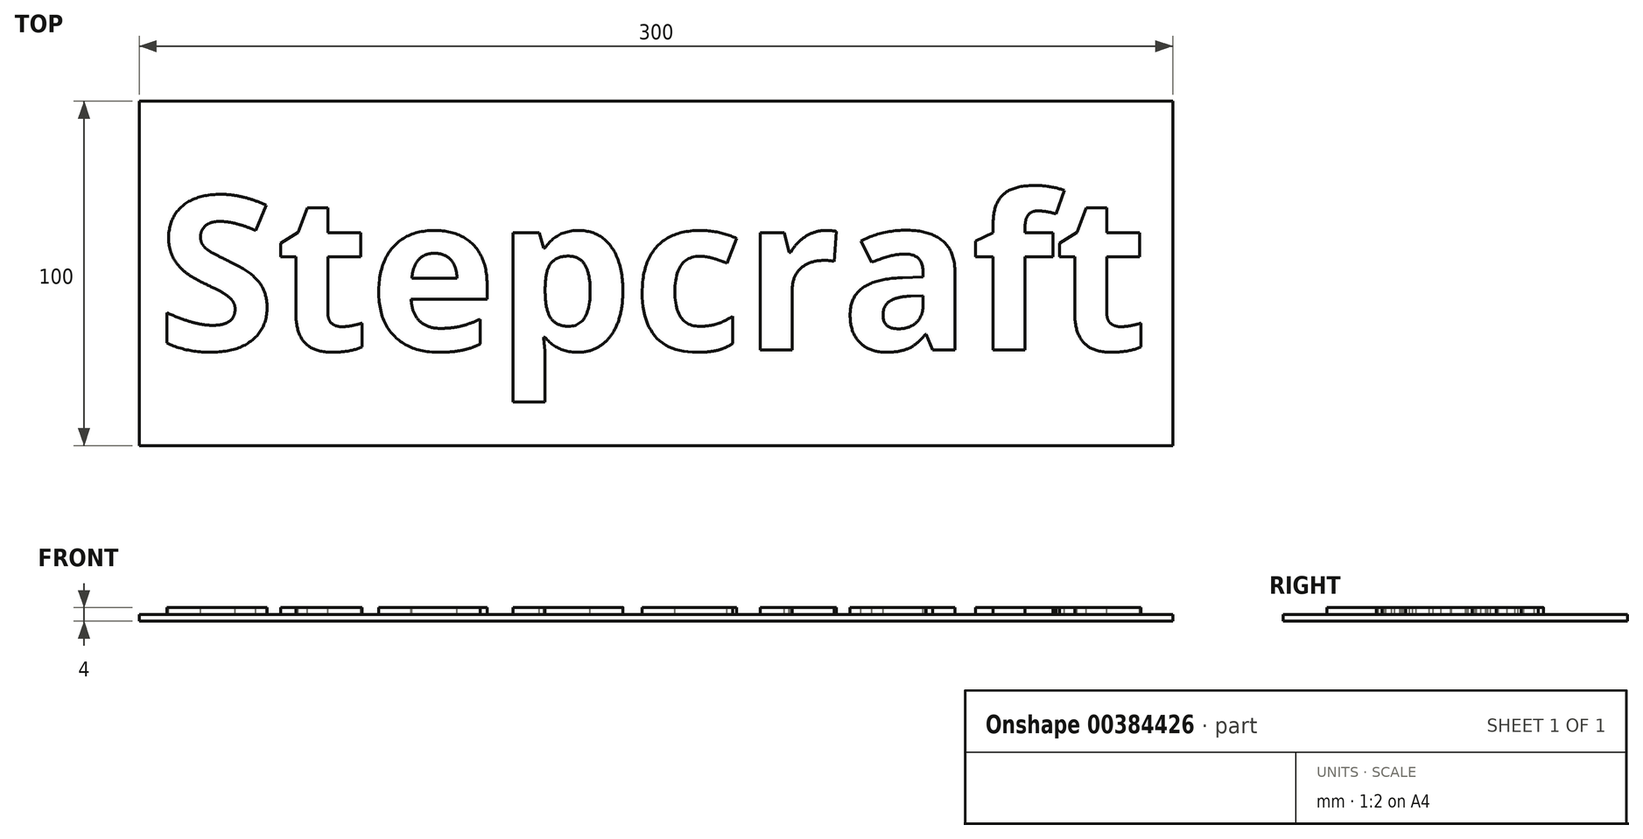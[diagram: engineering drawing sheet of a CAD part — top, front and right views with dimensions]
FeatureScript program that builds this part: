
annotation { "Feature Type Name" : "Feature", "Feature Type Description" : "" }
export const myFeature = defineFeature(function(context is Context, id is Id, definition is map)
    precondition{}
    {
        {
            var Q0;
            Q0=qCreatedBy(makeId("Top.planeOp"),FACE);
            var sketch = newSketch(context, id + "F0", { "sketchPlane" : qUnion([Q0])});
            skLineSegment(sketch, "E0.bottom", {"start": v(150, 50) * mm, "end": v(-150, 50) * mm});
            skLineSegment(sketch, "E0.top", {"start": v(150, -50) * mm, "end": v(-150, -50) * mm});
            skLineSegment(sketch, "E0.left", {"start": v(150, 50) * mm, "end": v(150, -50) * mm});
            skLineSegment(sketch, "E0.right", {"start": v(-150, 50) * mm, "end": v(-150, -50) * mm});
            skPoint(sketch, "E0.middle", {"position": v(0, 0) * mm});
            skText(sketch, "E1", { "text": "Stepcraft", "fontName": "OpenSans-Bold.ttf"});
            const initialGuessF0  = {"E1": [-0.14483, -0.02227, 1, 0, 0.045]};
            skSetInitialGuess(sketch, initialGuessF0);
            skSolve(sketch);
        }
        {
            var Q0;
            Q0 = qSketchRegion(id + "F0", true);
            var Q1;
            Q1=makeQuery(id+"F0.imprint","IMPRINT",FACE,{"disambiguationData":[TD([[makeQuery(id+"F0.imprint","IMPRINT",EDGE,{"derivedFrom":sQuery(id+"F0.wireOp",EDGE,"E1.sketch_text.stroke-103")}),-1.0]])]});
            var Q2;
            Q2=makeQuery(id+"F0.imprint","IMPRINT",FACE,{"disambiguationData":[TD([[makeQuery(id+"F0.imprint","IMPRINT",EDGE,{"derivedFrom":sQuery(id+"F0.wireOp",EDGE,"E1.sketch_text.stroke-134")}),1.0]])]});
            var Q3;
            Q3=makeQuery(id+"F0.imprint","IMPRINT",FACE,{"disambiguationData":[TD([[makeQuery(id+"F0.imprint","IMPRINT",EDGE,{"derivedFrom":sQuery(id+"F0.wireOp",EDGE,"E1.sketch_text.stroke-159")}),-1.0]])]});
            var Q4;
            Q4=makeQuery(id+"F0.imprint","IMPRINT",FACE,{"disambiguationData":[TD([[makeQuery(id+"F0.imprint","IMPRINT",EDGE,{"derivedFrom":sQuery(id+"F0.wireOp",EDGE,"E1.sketch_text.stroke-66")}),-1.0]])]});
            var Q5;
            Q5=makeQuery(id+"F0.imprint","IMPRINT",FACE,{"disambiguationData":[TD([[makeQuery(id+"F0.imprint","IMPRINT",EDGE,{"derivedFrom":sQuery(id+"F0.wireOp",EDGE,"E1.sketch_text.stroke-0")}),-1.0]])]});
            var Q6;
            Q6=makeQuery(id+"F0.imprint","IMPRINT",FACE,{"disambiguationData":[TD([[makeQuery(id+"F0.imprint","IMPRINT",EDGE,{"derivedFrom":sQuery(id+"F0.wireOp",EDGE,"E1.sketch_text.stroke-28")}),-1.0]])]});
            var Q7;
            Q7=makeQuery(id+"F0.imprint","IMPRINT",FACE,{"disambiguationData":[TD([[makeQuery(id+"F0.imprint","IMPRINT",EDGE,{"derivedFrom":sQuery(id+"F0.wireOp",EDGE,"E1.sketch_text.stroke-46")}),1.0]])]});
            var Q8;
            Q8=makeQuery(id+"F0.imprint","IMPRINT",FACE,{"disambiguationData":[TD([[makeQuery(id+"F0.imprint","IMPRINT",EDGE,{"derivedFrom":sQuery(id+"F0.wireOp",EDGE,"E1.sketch_text.stroke-81")}),1.0]])]});
            var Q9;
            Q9=makeQuery(id+"F0.imprint","IMPRINT",FACE,{"disambiguationData":[TD([[makeQuery(id+"F0.imprint","IMPRINT",EDGE,{"derivedFrom":sQuery(id+"F0.wireOp",EDGE,"E0.bottom")}),1.0]])]});
            var Q10;
            Q10=makeQuery(id+"F0.imprint","IMPRINT",FACE,{"disambiguationData":[TD([[makeQuery(id+"F0.imprint","IMPRINT",EDGE,{"derivedFrom":sQuery(id+"F0.wireOp",EDGE,"E1.sketch_text.stroke-89")}),-1.0]])]});
            var Q11;
            Q11=makeQuery(id+"F0.imprint","IMPRINT",FACE,{"disambiguationData":[TD([[makeQuery(id+"F0.imprint","IMPRINT",EDGE,{"derivedFrom":sQuery(id+"F0.wireOp",EDGE,"E1.sketch_text.stroke-141")}),-1.0]])]});
            var Q12;
            Q12=makeQuery(id+"F0.imprint","IMPRINT",FACE,{"disambiguationData":[TD([[makeQuery(id+"F0.imprint","IMPRINT",EDGE,{"derivedFrom":sQuery(id+"F0.wireOp",EDGE,"E1.sketch_text.stroke-46")}),-1.0]])]});
            var Q13;
            Q13=makeQuery(id+"F0.imprint","IMPRINT",FACE,{"disambiguationData":[TD([[makeQuery(id+"F0.imprint","IMPRINT",EDGE,{"derivedFrom":sQuery(id+"F0.wireOp",EDGE,"E1.sketch_text.stroke-116")}),-1.0]])]});
            extrude(context, id + "F1", {"entities" : qUnion([Q0, Q1, Q2, Q3, Q4, Q5, Q6, Q7, Q8, Q9, Q10, Q11, Q12, Q13]), "oppositeDirection" : true, "depth" : 4 * mm});
        }
        {
            var Q0;
            Q0=makeQuery(id+"F0.imprint","IMPRINT",FACE,{"disambiguationData":[TD([[makeQuery(id+"F0.imprint","IMPRINT",EDGE,{"derivedFrom":sQuery(id+"F0.wireOp",EDGE,"E1.sketch_text.stroke-46")}),1.0]])]});
            var Q1;
            Q1=makeQuery(id+"F0.imprint","IMPRINT",FACE,{"disambiguationData":[TD([[makeQuery(id+"F0.imprint","IMPRINT",EDGE,{"derivedFrom":sQuery(id+"F0.wireOp",EDGE,"E1.sketch_text.stroke-81")}),1.0]])]});
            var Q2;
            Q2=makeQuery(id+"F0.imprint","IMPRINT",FACE,{"disambiguationData":[TD([[makeQuery(id+"F0.imprint","IMPRINT",EDGE,{"derivedFrom":sQuery(id+"F0.wireOp",EDGE,"E1.sketch_text.stroke-134")}),1.0]])]});
            var Q3;
            Q3=makeQuery(id+"F0.imprint","IMPRINT",FACE,{"disambiguationData":[TD([[makeQuery(id+"F0.imprint","IMPRINT",EDGE,{"derivedFrom":sQuery(id+"F0.wireOp",EDGE,"E0.bottom")}),1.0]])]});
            extrude(context, id + "F2", {"entities" : qUnion([Q0, Q1, Q2, Q3]), "operationType" : NewBodyOperationType.REMOVE, "oppositeDirection" : true, "depth" : 2 * mm});
        }
    });
